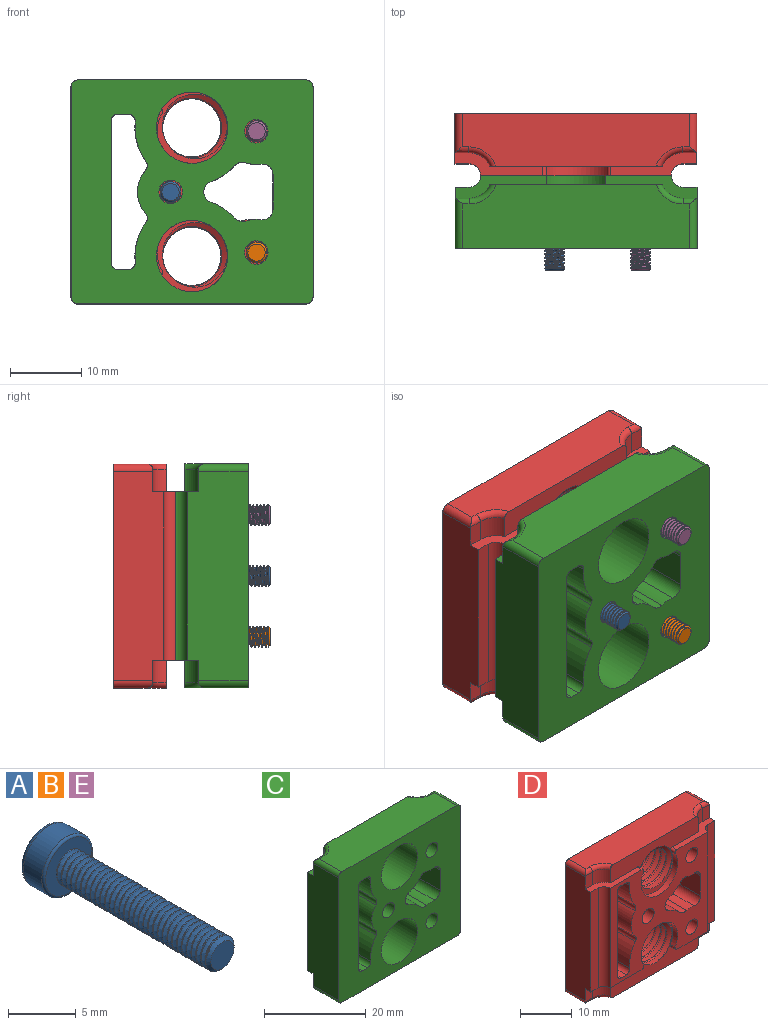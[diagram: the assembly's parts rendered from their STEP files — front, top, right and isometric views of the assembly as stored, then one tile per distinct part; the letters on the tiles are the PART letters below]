
ASSEMBLY  parts=5 mates=4
PART A: 19 faces, bbox 5.9x18.8x5.9 mm
  f0: cylinder r=1.18mm len=15.74mm, axis (0,-1,0), area -25.3mm2, adj f2,f3,f4,f9
  f1: cylinder r=1.46mm len=15.74mm, axis (0,-1,0), area 32.2mm2, adj f3,f4,f5,f9
  f2: plane 3.21x3.19mm, normal (0,1,0), area 1.3mm2, adj f0,f3,f4,f5
  f3: bspline ~16.07x2.93mm, area 86.2mm2, adj f0,f1,f2,f9
  f4: bspline ~16.36x3.93mm, area 119.3mm2, adj f0,f1,f2,f9
  f5: cone r=1.35mm half-angle=45deg, axis (0,1,0), area 3.1mm2, adj f1,f2,f6
  f6: plane 2.4x2.4mm, normal (0,-1,0), area 4.5mm2, adj f5
  f7: torus R=2.4mm, axis (0,1,0), area 5mm2, adj f8,f9
  f8: cylinder r=2.6mm len=5.2mm, axis (0,1,0), area 31mm2, adj f7,f10
  f9: plane 4.94x4.94mm, normal (0,-1,0), area 12.7mm2, adj f0,f1,f3,f4,f7
  f10: torus R=2.2mm, axis (0,1,0), area 9.7mm2, adj f8,f11
  f11: plane 4.4x4.4mm, normal (0,1,0), area 7.4mm2, adj f10,f12,f13,f14,f15,f16,f17
  f12: plane 1.7x1.5mm, normal (0.87,0,0.5), area 2.9mm2, adj f11,f13,f17,f18
  f13: plane 1.7x1.5mm, normal (0.87,0,-0.5), area 2.9mm2, adj f11,f12,f14,f18
  f14: plane 1.73x1.7mm, normal (0,0,-1), area 2.9mm2, adj f11,f13,f15,f18
  f15: plane 1.7x1.5mm, normal (-0.87,0,-0.5), area 2.9mm2, adj f11,f14,f16,f18
  f16: plane 1.7x1.5mm, normal (-0.87,0,0.5), area 2.9mm2, adj f11,f15,f17,f18
  f17: plane 1.73x1.7mm, normal (0,0,1), area 2.9mm2, adj f11,f12,f16,f18
  f18: plane 3.46x3mm, normal (0,1,0), area 7.8mm2, adj f12,f13,f14,f15,f16,f17
PART B: same geometry as A
PART C: 65 faces, bbox 34x10.3x31.5 mm
  f0: cylinder r=4.65mm len=10.2mm, axis (0,-1,0), area 67.7mm2, adj f1,f2,f29,f64
  f1: cylinder r=1mm len=10.2mm, axis (0,1,0), area 13.7mm2, adj f0,f2,f53,f64
  f2: plane 33.9x31.4mm, normal (0,-1,0), area 736.2mm2, adj f0,f1,f3,f5,f6,f11,f12,f15
  f3: cylinder r=1.65mm len=10.2mm, axis (0,-1,0), area 105.7mm2, adj f2,f64
  f4: plane 23.6x1.95mm, normal (0,1,0), area 46mm2, adj f5,f9,f10,f32
  f5: plane 29.4x8.55mm, normal (-1,0,0), area 242.4mm2, adj f2,f4,f7,f9,f27,f30,f32,f44
  f6: plane 10.2x4.82mm, normal (-1,0,0), area 49.1mm2, adj f2,f24,f41,f64
  f7: plane 3.1x1.95mm, normal (0,1,0), area 6mm2, adj f5,f8,f9,f22,f27
  f8: cylinder r=0.8mm len=1.93mm, axis (1,0,0), area 1.8mm2, adj f7,f19,f26,f27
  f9: plane 12.81x3.2mm, normal (0,0,1), area 19mm2, adj f4,f5,f7,f10,f18,f22,f54,f64
  f10: cylinder r=1.65mm len=23.6mm, axis (0,0,-1), area 61.2mm2, adj f4,f9,f32,f64
  f11: cylinder r=1mm len=7mm, axis (0,1,0), area 10.6mm2, adj f2,f12,f13,f21,f26
  f12: plane 29.4x8.55mm, normal (1,0,0), area 242.4mm2, adj f2,f11,f13,f14,f33,f34,f55,f57
  f13: plane 3.1x1.95mm, normal (0,1,0), area 6mm2, adj f11,f12,f21,f23,f55
  f14: plane 23.6x1.95mm, normal (0,1,0), area 46mm2, adj f12,f55,f56,f57
  f15: cylinder r=1mm len=10.2mm, axis (0,1,0), area 17mm2, adj f2,f16,f17,f64
  f16: plane 10.2x1.4mm, normal (0,0,-1), area 14.2mm2, adj f2,f15,f48,f64
  f17: cylinder r=8mm len=10.2mm, axis (0,-1,0), area 59.6mm2, adj f2,f15,f29,f64
  f18: plane 24.25x4mm, normal (0,1,0), area 81.1mm2, adj f9,f19,f20,f22,f23,f26,f54,f55
  f19: torus R=4mm, axis (0,0,1), area 5.3mm2, adj f8,f18,f22,f26
  f20: torus R=4mm, axis (0,0,1), area 5.3mm2, adj f18,f21,f23,f26
  f21: cylinder r=0.8mm len=1.93mm, axis (1,0,0), area 1.8mm2, adj f11,f13,f20,f26
  f22: cylinder r=3.2mm len=3.1mm, axis (0,0,-1), area 11.4mm2, adj f7,f9,f18,f19
  f23: cylinder r=3.2mm len=3.1mm, axis (0,0,-1), area 11.4mm2, adj f13,f18,f20,f55
  f24: cylinder r=1.5mm len=10.2mm, axis (0,-1,0), area 26.2mm2, adj f2,f6,f25,f64
  f25: cylinder r=4.65mm len=10.2mm, axis (0,-1,0), area 21.7mm2, adj f2,f24,f28,f64
  f26: plane 31.9x8.9mm, normal (0,0,1), area 263.9mm2, adj f2,f8,f11,f18,f19,f20,f21,f27
  f27: cylinder r=1mm len=7mm, axis (0,1,0), area 10.6mm2, adj f2,f5,f7,f8,f26
  f28: cylinder r=1.5mm len=10.2mm, axis (0,-1,0), area 17.7mm2, adj f2,f25,f58,f64
  f29: cylinder r=1mm len=10.2mm, axis (0,-1,0), area 13.7mm2, adj f0,f2,f17,f64
  f30: plane 3.1x1.95mm, normal (0,1,0), area 6mm2, adj f5,f31,f32,f39,f44
  f31: cylinder r=0.8mm len=1.93mm, axis (-1,0,0), area 1.8mm2, adj f30,f36,f43,f44
  f32: plane 12.81x3.2mm, normal (0,0,-1), area 19mm2, adj f4,f5,f10,f30,f35,f39,f45,f64
  f33: cylinder r=1mm len=7mm, axis (0,-1,0), area 10.6mm2, adj f2,f12,f34,f38,f43
  f34: plane 3.1x1.95mm, normal (0,1,0), area 6mm2, adj f12,f33,f38,f40,f57
  f35: plane 24.25x4mm, normal (0,1,0), area 81.1mm2, adj f32,f36,f37,f39,f40,f43,f45,f57
  f36: torus R=4mm, axis (0,0,-1), area 5.3mm2, adj f31,f35,f39,f43
  f37: torus R=4mm, axis (0,0,-1), area 5.3mm2, adj f35,f38,f40,f43
  f38: cylinder r=0.8mm len=1.93mm, axis (-1,0,0), area 1.8mm2, adj f33,f34,f37,f43
  f39: cylinder r=3.2mm len=3.1mm, axis (0,0,-1), area 11.4mm2, adj f30,f32,f35,f36
  f40: cylinder r=3.2mm len=3.1mm, axis (0,0,-1), area 11.4mm2, adj f34,f35,f37,f57
  f41: cylinder r=1.5mm len=10.2mm, axis (0,1,0), area 26.2mm2, adj f2,f6,f42,f64
  f42: cylinder r=4.65mm len=10.2mm, axis (0,1,0), area 21.7mm2, adj f2,f41,f63,f64
  f43: plane 31.9x8.9mm, normal (0,0,-1), area 263.9mm2, adj f2,f31,f33,f35,f36,f37,f38,f44
  f44: cylinder r=1mm len=7mm, axis (0,-1,0), area 10.6mm2, adj f2,f5,f30,f31,f43
  f45: cylinder r=5mm len=10.2mm, axis (0,-1,0), area 307.7mm2, adj f2,f32,f35,f57,f64
  f46: cylinder r=1.65mm len=10.2mm, axis (0,1,0), area 105.7mm2, adj f2,f64
  f47: cylinder r=1.65mm len=10.2mm, axis (0,-1,0), area 105.7mm2, adj f2,f64
  f48: cylinder r=1mm len=10.2mm, axis (0,1,0), area 16mm2, adj f2,f16,f49,f64
  f49: plane 19.8x10.2mm, normal (1,0,0), area 202mm2, adj f2,f48,f50,f64
  f50: cylinder r=1mm len=10.2mm, axis (0,-1,0), area 16mm2, adj f2,f49,f51,f64
  f51: plane 10.2x1.4mm, normal (0,0,1), area 14.2mm2, adj f2,f50,f52,f64
  f52: cylinder r=1mm len=10.2mm, axis (0,-1,0), area 17mm2, adj f2,f51,f53,f64
  f53: cylinder r=8mm len=10.2mm, axis (0,1,0), area 59.6mm2, adj f1,f2,f52,f64
  f54: cylinder r=5mm len=10.2mm, axis (0,1,0), area 307.7mm2, adj f2,f9,f18,f55,f64
  f55: plane 12.81x3.2mm, normal (0,0,1), area 19mm2, adj f12,f13,f14,f18,f23,f54,f56,f64
  f56: cylinder r=1.65mm len=23.6mm, axis (0,0,-1), area 61.2mm2, adj f14,f55,f57,f64
  f57: plane 12.81x3.2mm, normal (0,0,-1), area 19mm2, adj f12,f14,f34,f35,f40,f45,f56,f64
  f58: cylinder r=8mm len=10.2mm, axis (0,-1,0), area 41mm2, adj f2,f28,f59,f64
  f59: cylinder r=1.5mm len=10.2mm, axis (0,-1,0), area 19mm2, adj f2,f58,f60,f64
  f60: cylinder r=4.65mm len=10.2mm, axis (0,-1,0), area 0.6mm2, adj f2,f59,f61,f64
  f61: cylinder r=1.5mm len=10.2mm, axis (0,1,0), area 19mm2, adj f2,f60,f62,f64
  f62: cylinder r=8mm len=10.2mm, axis (0,1,0), area 41mm2, adj f2,f61,f63,f64
  f63: cylinder r=1.5mm len=10.2mm, axis (0,1,0), area 17.7mm2, adj f2,f42,f62,f64
  f64: plane 26.7x23.6mm, normal (0,1,0), area 328.3mm2, adj f0,f1,f3,f6,f9,f10,f15,f16
PART D: 88 faces, bbox 34.3x9.8x31.8 mm
  f0: plane 12.33x3.2mm, normal (0,0,1), area 18.4mm2, adj f10,f12,f16,f17,f20,f22,f25,f84
  f1: plane 12.07x3.2mm, normal (0,0,-1), area 18mm2, adj f10,f14,f15,f18,f19,f28,f29,f85
  f2: bspline ~9.67x8.37mm, area 57.8mm2, adj f3,f5,f9,f14
  f3: bspline ~11.55x10mm, area 133.9mm2, adj f2,f4,f9,f14,f43
  f4: cone r=3.86mm half-angle=45deg, axis (0,1,0), area 0.2mm2, adj f3,f5,f14,f43
  f5: bspline ~11.55x10mm, area 133.8mm2, adj f2,f4,f9,f14,f43
  f6: bspline ~11.55x10mm, area 133.9mm2, adj f7,f9,f12,f44,f45
  f7: bspline ~9.67x8.37mm, area 57.8mm2, adj f6,f8,f9,f12
  f8: bspline ~11.55x10mm, area 133.8mm2, adj f7,f9,f12,f44,f45
  f9: plane 34.32x31.82mm, normal (0,1,0), area 695.9mm2, adj f2,f3,f5,f6,f7,f8,f15,f20
  f10: plane 26.7x23.6mm, normal (0,-1,0), area 319.8mm2, adj f0,f1,f11,f13,f17,f18,f46,f47
  f11: plane 12.07x3.2mm, normal (0,0,1), area 18mm2, adj f10,f12,f15,f18,f19,f23,f24,f87
  f12: plane 24.54x12.56mm, normal (0,-1,0), area 99.3mm2, adj f0,f6,f7,f8,f11,f21,f24,f25
  f13: plane 12.33x3.2mm, normal (0,0,-1), area 18.4mm2, adj f10,f14,f16,f17,f20,f27,f30,f86
  f14: plane 24.55x12.57mm, normal (0,-1,0), area 99.3mm2, adj f1,f2,f3,f4,f5,f13,f26,f29
  f15: plane 29.4x7.05mm, normal (1,0,0), area 198.3mm2, adj f1,f9,f11,f19,f23,f28,f39,f42
  f16: plane 23.6x1.95mm, normal (0,-1,0), area 46mm2, adj f0,f13,f17,f20
  f17: cylinder r=1.65mm len=23.6mm, axis (0,0,-1), area 61.2mm2, adj f0,f10,f13,f16
  f18: cylinder r=1.65mm len=23.6mm, axis (0,0,-1), area 61.2mm2, adj f1,f10,f11,f19
  f19: plane 23.6x1.95mm, normal (0,-1,0), area 46mm2, adj f1,f11,f15,f18
  f20: plane 29.4x7.05mm, normal (-1,0,0), area 198.3mm2, adj f0,f9,f13,f16,f22,f27,f40,f41
  f21: plane 31.9x7.4mm, normal (0,0,1), area 216mm2, adj f9,f12,f35,f36,f37,f38,f41,f42
  f22: plane 3.1x1.95mm, normal (0,-1,0), area 6mm2, adj f0,f20,f25,f36,f41
  f23: plane 3.1x1.95mm, normal (0,-1,0), area 6mm2, adj f11,f15,f24,f38,f42
  f24: cylinder r=3.2mm len=3.1mm, axis (0,0,1), area 11.4mm2, adj f11,f12,f23,f37
  f25: cylinder r=3.2mm len=3.1mm, axis (0,0,1), area 11.4mm2, adj f0,f12,f22,f35
  f26: plane 31.9x7.4mm, normal (0,0,-1), area 216mm2, adj f9,f14,f31,f32,f33,f34,f39,f40
  f27: plane 3.1x1.95mm, normal (0,-1,0), area 6mm2, adj f13,f20,f30,f34,f40
  f28: plane 3.1x1.95mm, normal (0,-1,0), area 6mm2, adj f1,f15,f29,f32,f39
  f29: cylinder r=3.2mm len=3.1mm, axis (0,0,-1), area 11.4mm2, adj f1,f14,f28,f31
  f30: cylinder r=3.2mm len=3.1mm, axis (0,0,-1), area 11.4mm2, adj f13,f14,f27,f33
  f31: torus R=4mm, axis (0,0,-1), area 5.3mm2, adj f14,f26,f29,f32
  f32: cylinder r=0.8mm len=1.93mm, axis (1,0,0), area 1.8mm2, adj f26,f28,f31,f39
  f33: torus R=4mm, axis (0,0,-1), area 5.3mm2, adj f14,f26,f30,f34
  f34: cylinder r=0.8mm len=1.93mm, axis (1,0,0), area 1.8mm2, adj f26,f27,f33,f40
  f35: torus R=4mm, axis (0,0,1), area 5.3mm2, adj f12,f21,f25,f36
  f36: cylinder r=0.8mm len=1.93mm, axis (1,0,0), area 1.8mm2, adj f21,f22,f35,f41
  f37: torus R=4mm, axis (0,0,1), area 5.3mm2, adj f12,f21,f24,f38
  f38: cylinder r=0.8mm len=1.93mm, axis (1,0,0), area 1.8mm2, adj f21,f23,f37,f42
  f39: cylinder r=1mm len=5.5mm, axis (0,-1,0), area 8.2mm2, adj f9,f15,f26,f28,f32
  f40: cylinder r=1mm len=5.5mm, axis (0,1,0), area 8.2mm2, adj f9,f20,f26,f27,f34
  f41: cylinder r=1mm len=5.5mm, axis (0,1,0), area 8.2mm2, adj f9,f20,f21,f22,f36
  f42: cylinder r=1mm len=5.5mm, axis (0,-1,0), area 8.2mm2, adj f9,f15,f21,f23,f38
  f43: cylinder r=5mm len=10mm, axis (0,-1,0), area 27.7mm2, adj f3,f4,f5,f9
  f44: cylinder r=5mm len=10mm, axis (0,-1,0), area 27.7mm2, adj f6,f8,f9,f45
  f45: cone r=3.86mm half-angle=45deg, axis (0,1,0), area 0.3mm2, adj f6,f8,f12,f44,f76,f87
  f46: plane 19.8x8.7mm, normal (1,0,0), area 172.3mm2, adj f9,f10,f47,f57
  f47: cylinder r=1mm len=8.7mm, axis (0,1,0), area 13.8mm2, adj f9,f10,f46,f48
  f48: plane 8.7x1.4mm, normal (0,0,-1), area 12.1mm2, adj f9,f10,f47,f49
  f49: cylinder r=1mm len=8.7mm, axis (0,1,0), area 14.5mm2, adj f9,f10,f48,f50
  f50: cylinder r=8mm len=8.7mm, axis (0,1,0), area 50.8mm2, adj f9,f10,f49,f51
  f51: cylinder r=1mm len=8.7mm, axis (0,1,0), area 11.7mm2, adj f9,f10,f50,f52
  f52: cylinder r=4.65mm len=8.7mm, axis (0,1,0), area 57.7mm2, adj f9,f10,f51,f53
  f53: cylinder r=1mm len=8.7mm, axis (0,1,0), area 11.7mm2, adj f9,f10,f52,f54
  f54: cylinder r=8mm len=8.7mm, axis (0,1,0), area 50.8mm2, adj f9,f10,f53,f55
  f55: cylinder r=1mm len=8.7mm, axis (0,1,0), area 14.5mm2, adj f9,f10,f54,f56
  f56: plane 8.7x1.4mm, normal (0,0,1), area 12.1mm2, adj f9,f10,f55,f57
  f57: cylinder r=1mm len=8.7mm, axis (0,1,0), area 13.8mm2, adj f9,f10,f46,f56
  f58: cylinder r=1.5mm len=8.7mm, axis (0,1,0), area 22.3mm2, adj f9,f10,f59,f69
  f59: plane 8.7x4.82mm, normal (-1,0,0), area 41.9mm2, adj f9,f10,f58,f60
  f60: cylinder r=1.5mm len=8.7mm, axis (0,1,0), area 22.3mm2, adj f9,f10,f59,f61
  f61: cylinder r=4.65mm len=8.7mm, axis (0,1,0), area 18.4mm2, adj f9,f10,f60,f62
  f62: cylinder r=1.5mm len=8.7mm, axis (0,1,0), area 14.7mm2, adj f9,f10,f61,f63
  f63: cylinder r=8mm len=8.7mm, axis (0,1,0), area 34.9mm2, adj f9,f10,f62,f64
  f64: cylinder r=1.5mm len=8.7mm, axis (0,1,0), area 16.2mm2, adj f9,f10,f63,f65
  f65: plane 8.7x0.06mm, normal (1,0,0), area 0.5mm2, adj f9,f10,f64,f66
  f66: cylinder r=1.5mm len=8.7mm, axis (0,1,0), area 16.2mm2, adj f9,f10,f65,f67
  f67: cylinder r=8mm len=8.7mm, axis (0,1,0), area 34.9mm2, adj f9,f10,f66,f68
  f68: cylinder r=1.5mm len=8.7mm, axis (0,1,0), area 15.1mm2, adj f9,f10,f67,f69
  f69: cylinder r=4.65mm len=8.7mm, axis (0,1,0), area 18.5mm2, adj f9,f10,f58,f68
  f70: cylinder r=3.15mm len=6.3mm, axis (0,1,0), area 118.8mm2, adj f9,f71
  f71: plane 6.3x6.3mm, normal (0,1,0), area 31.2mm2, adj f70
  f72: cylinder r=3.15mm len=6.3mm, axis (0,1,0), area 118.8mm2, adj f9,f73
  f73: plane 6.3x6.3mm, normal (0,1,0), area 31.2mm2, adj f72
  f74: cylinder r=3.15mm len=6.3mm, axis (0,1,0), area 118.8mm2, adj f9,f75
  f75: plane 6.3x6.3mm, normal (0,1,0), area 31.2mm2, adj f74
  f76: cylinder r=5mm len=10mm, axis (0,-1,0), area 27.3mm2, adj f10,f12,f45,f84,f87
  f77: cylinder r=5mm len=10mm, axis (0,-1,0), area 27.3mm2, adj f10,f14,f85,f86
  f78: cylinder r=1.65mm len=3.3mm, axis (0,-1,0), area 23.8mm2, adj f10,f79
  f79: plane 3.3x3.3mm, normal (0,-1,0), area 8.6mm2, adj f78
  f80: cylinder r=1.65mm len=3.3mm, axis (0,-1,0), area 23.8mm2, adj f10,f81
  f81: plane 3.3x3.3mm, normal (0,-1,0), area 8.6mm2, adj f80
  f82: cylinder r=1.65mm len=3.3mm, axis (0,-1,0), area 23.8mm2, adj f10,f83
  f83: plane 3.3x3.3mm, normal (0,-1,0), area 8.6mm2, adj f82
  f84: cylinder r=0.5mm len=1.3mm, axis (0,-1,0), area 1.4mm2, adj f0,f10,f12,f76
  f85: cylinder r=0.5mm len=1.3mm, axis (0,-1,0), area 1.4mm2, adj f1,f10,f14,f77
  f86: cylinder r=0.5mm len=1.3mm, axis (0,-1,0), area 1.4mm2, adj f10,f13,f14,f77
  f87: cylinder r=0.5mm len=1.3mm, axis (0,-1,0), area 1.4mm2, adj f10,f11,f12,f45,f76
PART E: same geometry as A
PLACE A t=(7.36,44.03,1.68)mm
PLACE B t=(19.42,44.03,-6.8)mm
PLACE C t=(10.39,27.25,1.71)mm
PLACE D t=(10.34,27.43,1.68)mm
PLACE E t=(19.42,44.03,10.2)mm
MATE fastened E.f9 <-> D.f70  axis (0,-1,0) through (19.36,44.03,10.18)mm
MATE fastened C.f3 <-> D.f52  axis (0,1,0) through (7.39,41.33,1.71)mm
MATE fastened B.f9 <-> D.f72  axis (0,-1,0) through (19.36,44.03,-6.82)mm
MATE fastened A.f0 <-> D.f74  axis (0,-1,0) through (7.36,44.03,1.68)mm
